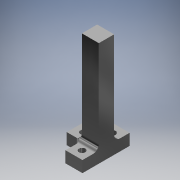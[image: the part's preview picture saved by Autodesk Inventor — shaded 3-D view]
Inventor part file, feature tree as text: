
AUTODESK INVENTOR PART (.ipt)
format: ipt  version: 2018 (Build 220112000, 112)  size: 232,960 bytes
history: native  units: mm
features: extrude x5, sketch x5, other x4, projected_geometry x3, reference x2, fillet x1
ambient origin geometry x8: Origin, YZ Plane, XZ Plane, XY Plane, X Axis, Y Axis, Z Axis, Center Point
bodies: Volumenkörper1 (feature_tree)
feature tree (20):
  extrude  "Extrusion1"  Depth=25.0mm
  extrude  "Extrusion2"  Depth=4.5mm
  extrude  "Extrusion3"  Depth=8.0mm
  fillet  "Rundung2"  Radius=75.0mm
  extrude  "Extrusion4"  Depth=75.0mm TaperAngle=0.0deg
  extrude  "Extrusion5"  Depth=10.0mm
  sketch  "Skizze1"  dims[d0=9.0mm d1=25.0mm]
  reference  "Referenz1"
  sketch  "Skizze2"  dims[d2=4.5mm d3=4.5mm]
  projected_geometry  "Projizierte Kontur1"
  projected_geometry  "Projizierte Kontur2"
  sketch  "Skizze3"  dims[d4=25.0mm d5=8.0mm d6=75.0mm d7=0.0mm]
  projected_geometry  "Projizierte Kontur3"
  reference  "Referenz2"
  sketch  "Skizze4"  dims[d8=6.0mm d9=75.0mm d10=0.0mm]
  sketch  "Skizze5"  dims[d12=75.0mm d13=0.0mm d14=5.2mm d16=3.0mm d17=10.0mm d18=0.0mm d19=10.0mm d20=0.0mm d21=3.4mm]
  other  "<userpath>\OneDrive\Development\Mohne\03_Konstruktion\Mohne komplett.iam"
  other  "Mohne komplett.iam"
  other  "chassis mit motorlöcher:1"
  other  "Wheel ALL1_MIR:1"
